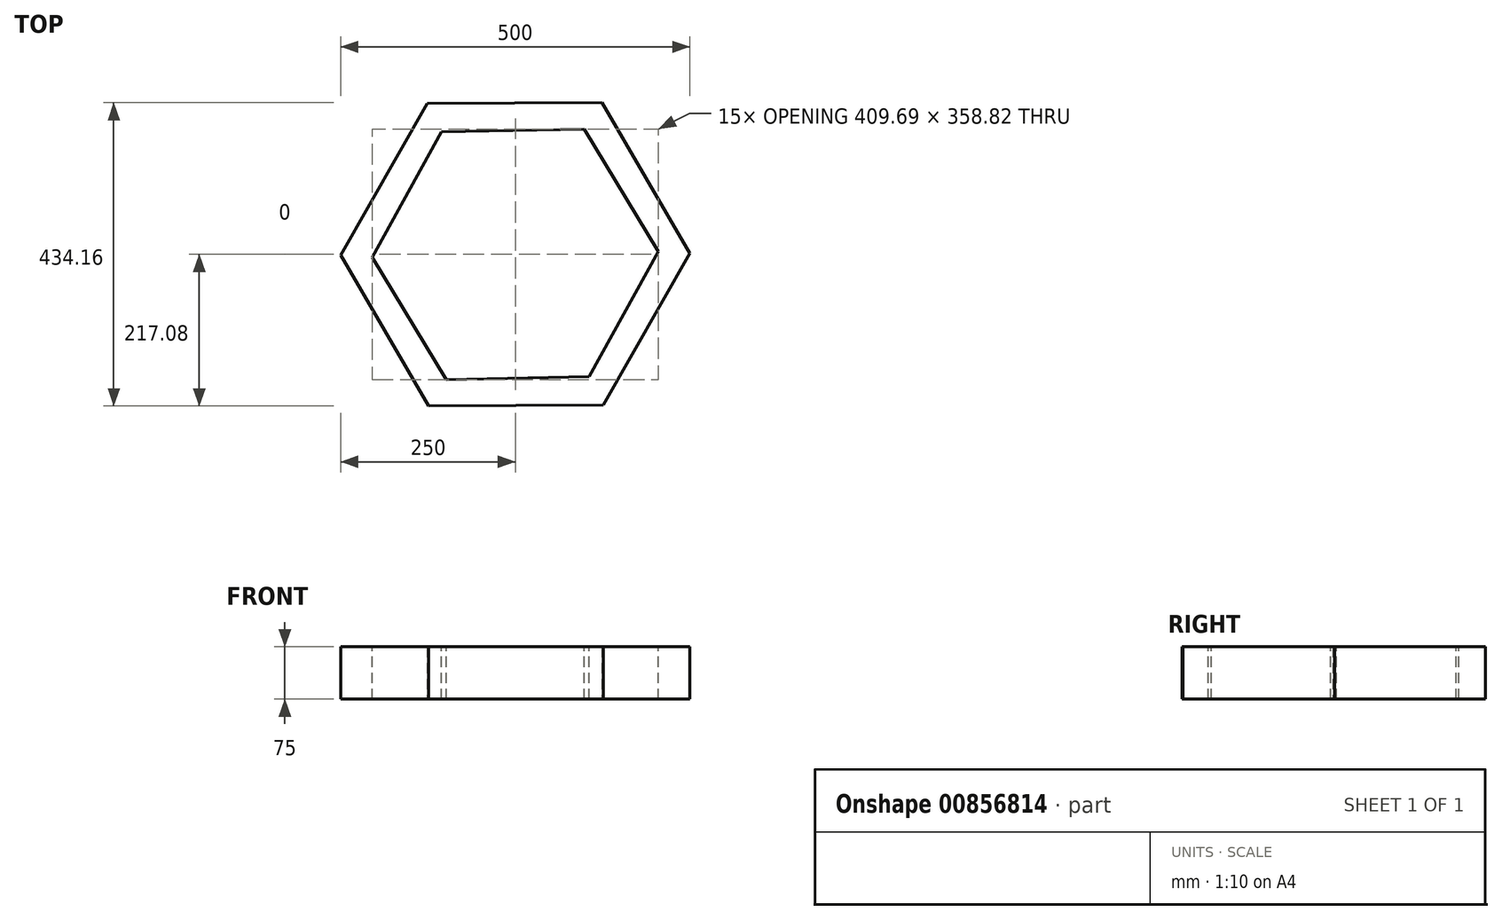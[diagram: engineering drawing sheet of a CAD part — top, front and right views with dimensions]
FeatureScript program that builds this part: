
annotation { "Feature Type Name" : "Feature", "Feature Type Description" : "" }
export const myFeature = defineFeature(function(context is Context, id is Id, definition is map)
    precondition{}
    {
        {
            var Q0;
            Q0=qCreatedBy(makeId("Top.planeOp"),FACE);
            var sketch = newSketch(context, id + "F0", { "sketchPlane" : qUnion([Q0])});
            skCircle(sketch, "E0.cCircle", {"center": v(0, 0) * mm, "radius": 216.5 * mm, "construction": true});
            skLineSegment(sketch, "E0.0", {"start": v(-250, -1.16) * mm, "end": v(-126, 215.92) * mm});
            skLineSegment(sketch, "E0.1", {"start": v(-126, 215.92) * mm, "end": v(124, 217.08) * mm});
            skLineSegment(sketch, "E0.2", {"start": v(124, 217.08) * mm, "end": v(250, 1.16) * mm});
            skLineSegment(sketch, "E0.3", {"start": v(250, 1.16) * mm, "end": v(126, -215.92) * mm});
            skLineSegment(sketch, "E0.4", {"start": v(126, -215.92) * mm, "end": v(-124, -217.08) * mm});
            skLineSegment(sketch, "E0.5", {"start": v(-124, -217.08) * mm, "end": v(-250, -1.16) * mm});
            skPoint(sketch, "E0.0.midPoint", {"position": v(-188, 107.38) * mm});
            skSolve(sketch);
        }
        {
            var Q0;
            Q0=makeQuery(id+"F0.imprint","IMPRINT",FACE,{"disambiguationData":[TD([[makeQuery(id+"F0.imprint","IMPRINT",EDGE,{"derivedFrom":sQuery(id+"F0.wireOp",EDGE,"E0.0")}),-1.0]])]});
            extrude(context, id + "F1", {"entities" : qUnion([Q0]), "depth" : 75 * mm, "offsetDistance" : 25.4 * mm});
        }
        {
            var Q0;
            Q0=makeQuery(id+"F1.opExtrude","CAP_FACE",FACE,{"disambiguationData":[OSD([sQuery(id+"F0.wireOp",EDGE,"E0.0"),sQuery(id+"F0.wireOp",EDGE,"E0.1"),sQuery(id+"F0.wireOp",EDGE,"E0.2"),sQuery(id+"F0.wireOp",EDGE,"E0.3"),sQuery(id+"F0.wireOp",EDGE,"E0.4"),sQuery(id+"F0.wireOp",EDGE,"E0.5")])],"isStart":false});
            var sketch = newSketch(context, id + "F2", { "sketchPlane" : qUnion([Q0])});
            skCircle(sketch, "E1.cCircle", {"center": v(0, 0) * mm, "radius": 177.43 * mm, "construction": true});
            skLineSegment(sketch, "E1.0", {"start": v(-204.84, -4.02) * mm, "end": v(-105.9, 175.39) * mm});
            skLineSegment(sketch, "E1.1", {"start": v(-105.9, 175.39) * mm, "end": v(98.94, 179.41) * mm});
            skLineSegment(sketch, "E1.2", {"start": v(98.94, 179.41) * mm, "end": v(204.84, 4.02) * mm});
            skLineSegment(sketch, "E1.3", {"start": v(204.84, 4.02) * mm, "end": v(105.9, -175.39) * mm});
            skLineSegment(sketch, "E1.4", {"start": v(105.9, -175.39) * mm, "end": v(-98.94, -179.41) * mm});
            skLineSegment(sketch, "E1.5", {"start": v(-98.94, -179.41) * mm, "end": v(-204.84, -4.02) * mm});
            skPoint(sketch, "E1.0.midPoint", {"position": v(-155.37, 85.68) * mm});
            skSolve(sketch);
        }
        {
            var Q0;
            Q0=makeQuery(id+"F2.imprint","IMPRINT",FACE,{"disambiguationData":[TD([[makeQuery(id+"F2.imprint","IMPRINT",EDGE,{"derivedFrom":sQuery(id+"F2.wireOp",EDGE,"E1.0")}),-1.0]])]});
            extrude(context, id + "F3", {"entities" : qUnion([Q0]), "operationType" : NewBodyOperationType.REMOVE, "oppositeDirection" : true, "depth" : 24.7 * mm, "offsetDistance" : 25.4 * mm});
        }
        {
            var Q0;
            Q0=makeQuery(id+"F3.boolean.opBoolean","COPY",FACE,{"derivedFrom":makeQuery(id+"F3.opExtrude","CAP_FACE",FACE,{"disambiguationData":[OSD([sQuery(id+"F2.wireOp",EDGE,"E1.0"),sQuery(id+"F2.wireOp",EDGE,"E1.1"),sQuery(id+"F2.wireOp",EDGE,"E1.2"),sQuery(id+"F2.wireOp",EDGE,"E1.3"),sQuery(id+"F2.wireOp",EDGE,"E1.4"),sQuery(id+"F2.wireOp",EDGE,"E1.5")])],"isStart":false})});
            extrude(context, id + "F4", {"entities" : qUnion([Q0]), "operationType" : NewBodyOperationType.REMOVE, "oppositeDirection" : true, "depth" : 15.24 * mm, "offsetDistance" : 25.4 * mm});
        }
        {
            var Q0;
            Q0=makeQuery(id+"F4.boolean.opBoolean","COPY",FACE,{"derivedFrom":makeQuery(id+"F4.opExtrude","CAP_FACE",FACE,{"disambiguationData":[OSD([sQuery(id+"F2.wireOp",EDGE,"E1.0"),sQuery(id+"F2.wireOp",EDGE,"E1.1"),sQuery(id+"F2.wireOp",EDGE,"E1.2"),sQuery(id+"F2.wireOp",EDGE,"E1.3"),sQuery(id+"F2.wireOp",EDGE,"E1.4"),sQuery(id+"F2.wireOp",EDGE,"E1.5")])],"isStart":false})});
            extrude(context, id + "F5", {"entities" : qUnion([Q0]), "operationType" : NewBodyOperationType.REMOVE, "oppositeDirection" : true, "depth" : 75 * mm, "offsetDistance" : 25.4 * mm});
        }
    });
